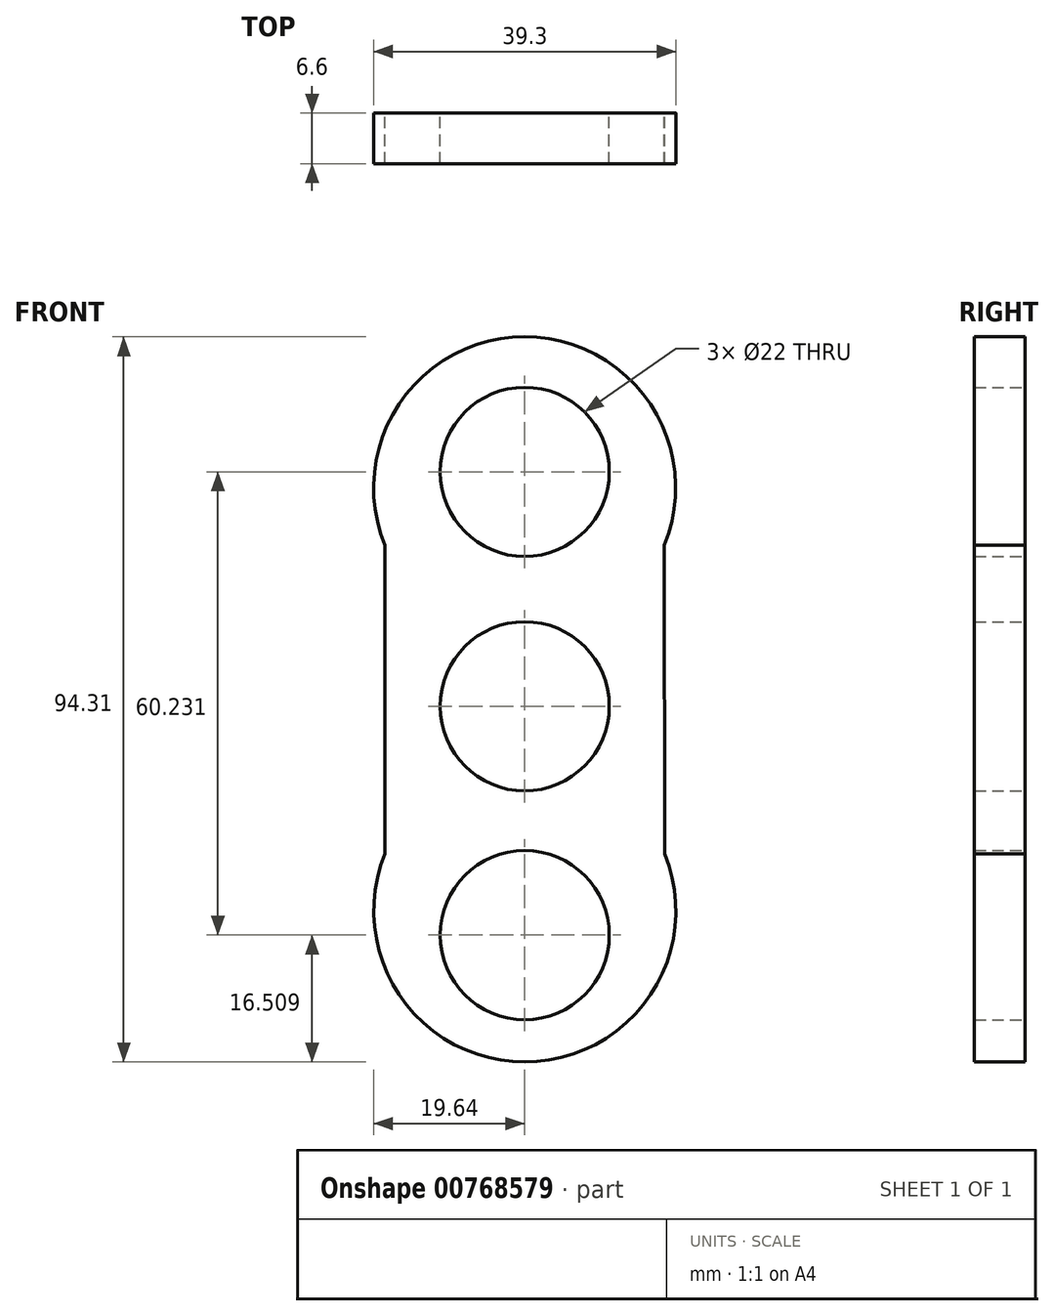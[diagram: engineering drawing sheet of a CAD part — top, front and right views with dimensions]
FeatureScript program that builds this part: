
annotation { "Feature Type Name" : "Feature", "Feature Type Description" : "" }
export const myFeature = defineFeature(function(context is Context, id is Id, definition is map)
    precondition{}
    {
        {
            var Q0;
            Q0=qCreatedBy(makeId("Front.planeOp"),FACE);
            var sketch = newSketch(context, id + "F0", { "sketchPlane" : qUnion([Q0])});
            skCircle(sketch, "E0", {"center": v(0, 30.48) * mm, "radius": 11 * mm});
            skCircle(sketch, "E1", {"center": v(0, 0) * mm, "radius": 11 * mm});
            skCircle(sketch, "E2", {"center": v(0, -29.75) * mm, "radius": 11 * mm});
            skArc(sketch, "E3", {"start": v(-18.16, -19.19) * mm, "mid": v(0.02, -46.26) * mm, "end": v(18.2, -19.19) * mm});
            skArc(sketch, "E4", {"start": v(18.16, 20.94) * mm, "mid": v(0, 48.05) * mm, "end": v(-18.16, 20.94) * mm});
            skLineSegment(sketch, "E5", {"start": v(-18.16, 20.94) * mm, "end": v(-18.16, -19.19) * mm});
            skLineSegment(sketch, "E6", {"start": v(18.16, 20.94) * mm, "end": v(18.2, -19.19) * mm});
            skSolve(sketch);
        }
        {
            var Q0;
            Q0 = qSketchRegion(id + "F0", true);
            extrude(context, id + "F1", {"entities" : qUnion([Q0]), "depth" : 6.6 * mm, "offsetDistance" : 25.4 * mm});
        }
    });
